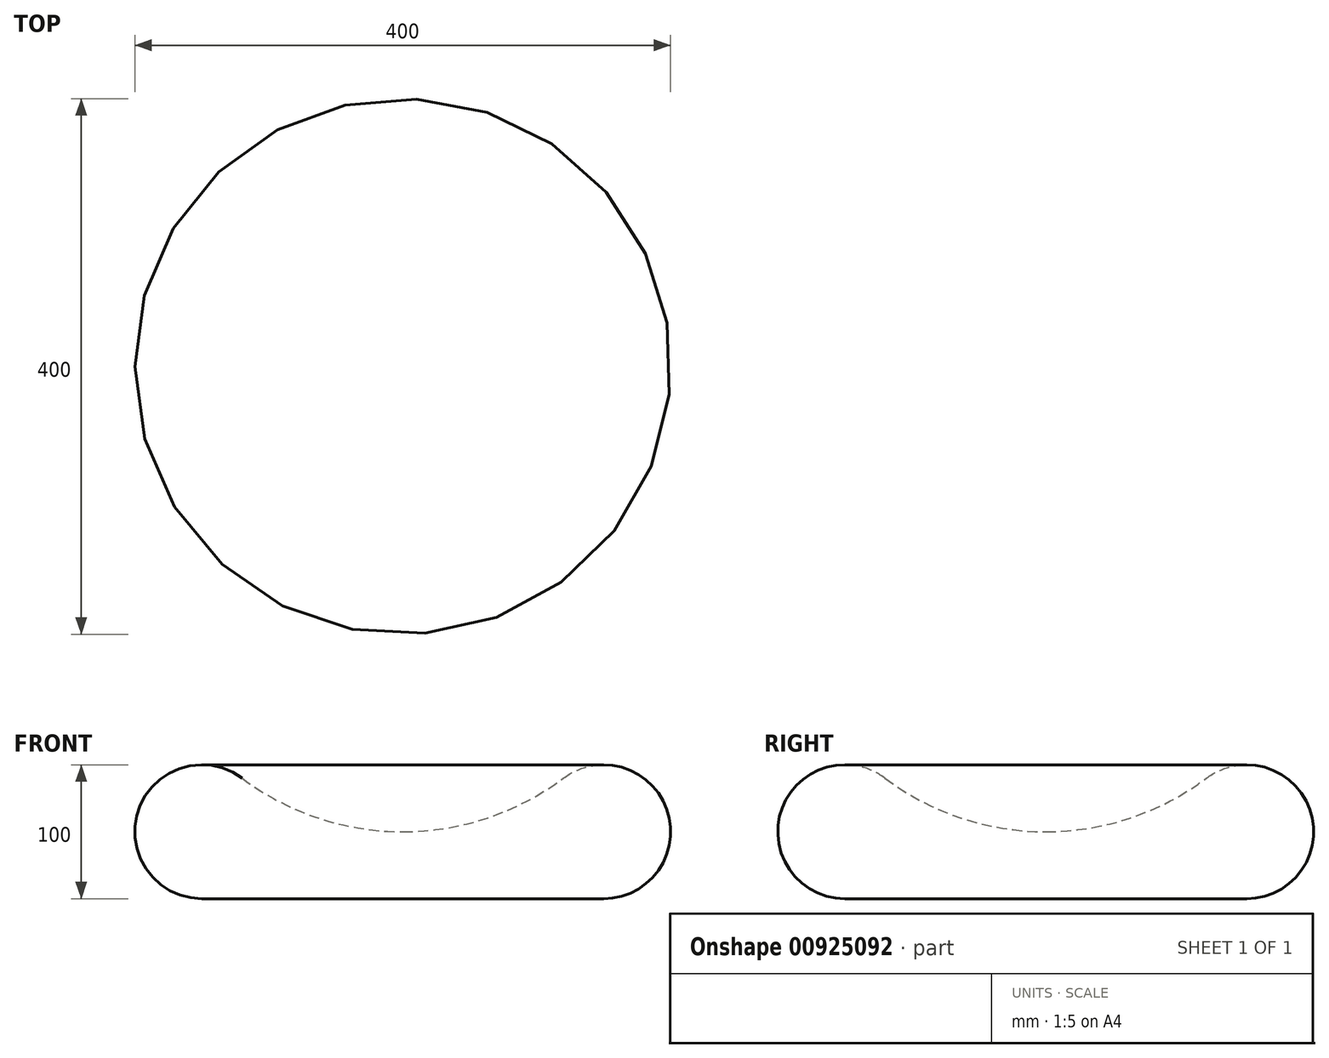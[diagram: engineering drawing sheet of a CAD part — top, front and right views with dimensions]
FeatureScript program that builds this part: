
annotation { "Feature Type Name" : "Feature", "Feature Type Description" : "" }
export const myFeature = defineFeature(function(context is Context, id is Id, definition is map)
    precondition{}
    {
        {
            var Q0;
            Q0=qCreatedBy(makeId("Front.planeOp"),FACE);
            var sketch = newSketch(context, id + "F0", { "sketchPlane" : qUnion([Q0])});
            skArc(sketch, "E0", {"start": v(-120, 90) * mm, "mid": v(-197.43, 65.81) * mm, "end": v(-150, 0) * mm});
            skArc(sketch, "E1", {"start": v(-120, 90) * mm, "mid": v(-63.25, 60.26) * mm, "end": v(0, 50) * mm});
            skLineSegment(sketch, "E2", {"start": v(-150, 0) * mm, "end": v(0, 0) * mm});
            skLineSegment(sketch, "E3", {"start": v(0, 0) * mm, "end": v(0, 50) * mm});
            skSolve(sketch);
        }
        {
            var Q0;
            Q0=makeQuery(id+"F0.imprint","IMPRINT",FACE,{"disambiguationData":[TD([[makeQuery(id+"F0.imprint","IMPRINT",EDGE,{"derivedFrom":sQuery(id+"F0.wireOp",EDGE,"E0")}),1.0]])]});
            var Q1;
            Q1=sQuery(id+"F0.wireOp",EDGE,"E3");
            revolve(context, id + "F1", {"surfaceOperationType" : NewSurfaceOperationType.NEW, "entities" : qUnion([Q0]), "axis" : qUnion([Q1]), "revolveType" : RevolveType.FULL});
        }
    });
